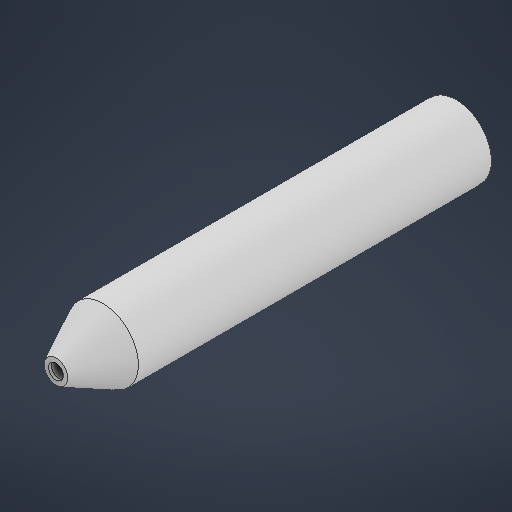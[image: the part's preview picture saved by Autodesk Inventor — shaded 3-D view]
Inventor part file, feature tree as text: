
AUTODESK INVENTOR PART (.ipt)
format: ipt  version: 2025.3 (Build 293356000, 356)  size: 201,216 bytes
history: native  units: in
note: dims shown in document units (in); Inventor stores cm internally (conversion verified against a paired STEP export)
features: other x3, extrude x1, sketch x1
ambient origin geometry x8: Origin, YZ Plane, XZ Plane, XY Plane, X Axis, Y Axis, Z Axis, Center Point
bodies: Solid1 (feature_tree)
feature tree (5):
  other  "Nozzle.ipt"
  extrude  "Extrusion1"  Depth=0.3937in
  other  "Solid1::Nozzle.ipt"
  other  "TaggingFeature1"
  sketch  "Sketch1"  dims[d0=0.3937in d1=0.0492in d2=0.3937in d3=0.0in]
